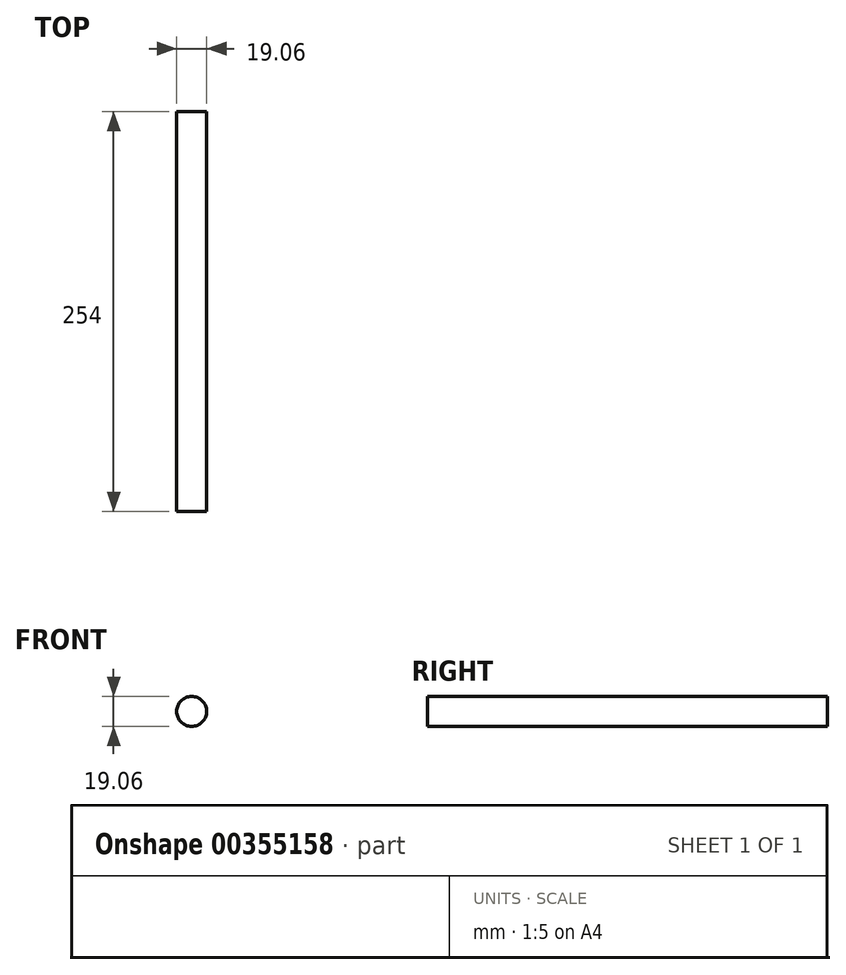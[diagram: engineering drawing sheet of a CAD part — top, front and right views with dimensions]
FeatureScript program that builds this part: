
annotation { "Feature Type Name" : "Feature", "Feature Type Description" : "" }
export const myFeature = defineFeature(function(context is Context, id is Id, definition is map)
    precondition{}
    {
        {
            var Q0;
            Q0=qCreatedBy(makeId("Front.planeOp"),FACE);
            var sketch = newSketch(context, id + "F0", { "sketchPlane" : qUnion([Q0])});
            skCircle(sketch, "E0", {"center": v(0, 0) * mm, "radius": 9.53 * mm});
            skSolve(sketch);
        }
        {
            var Q0;
            Q0 = qSketchRegion(id + "F0", true);
            extrude(context, id + "F1", {"entities" : qUnion([Q0]), "depth" : 254 * mm});
        }
    });
